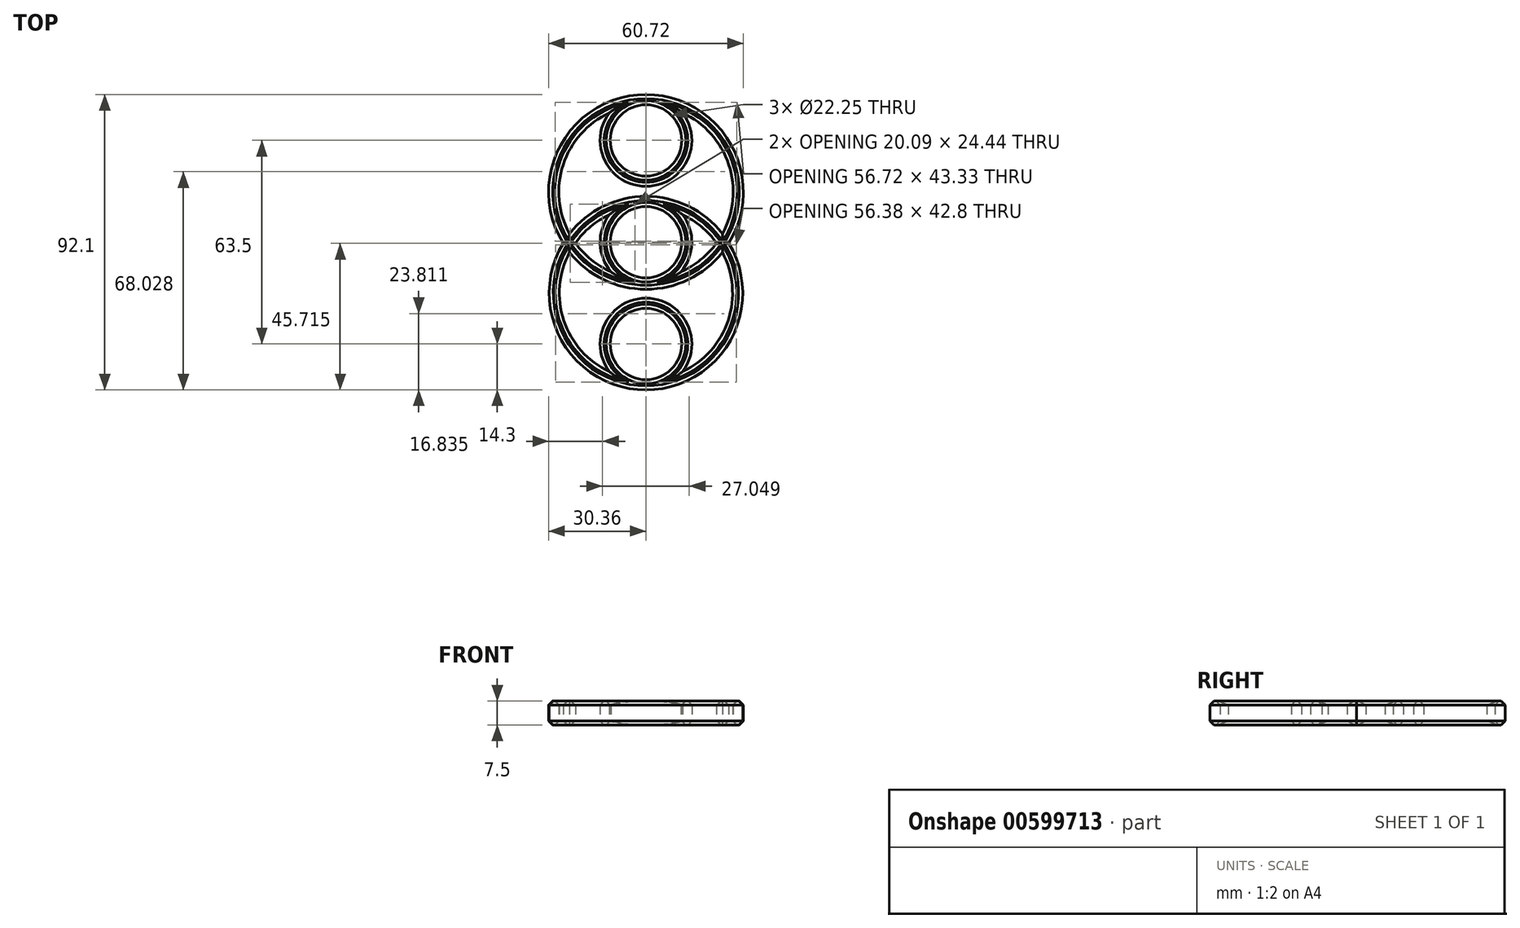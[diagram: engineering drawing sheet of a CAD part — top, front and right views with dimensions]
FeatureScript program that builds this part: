
annotation { "Feature Type Name" : "Feature", "Feature Type Description" : "" }
export const myFeature = defineFeature(function(context is Context, id is Id, definition is map)
    precondition{}
    {
        {
            var Q0;
            Q0=qCreatedBy(makeId("Top.planeOp"),FACE);
            var sketch = newSketch(context, id + "F0", { "sketchPlane" : qUnion([Q0])});
            skCircle(sketch, "E0", {"center": v(0, 0) * mm, "radius": 11.12 * mm});
            skCircle(sketch, "E1", {"center": v(0, 31.75) * mm, "radius": 11.12 * mm});
            skCircle(sketch, "E2", {"center": v(0, -31.75) * mm, "radius": 11.12 * mm});
            skCircle(sketch, "E3", {"center": v(0, 31.75) * mm, "radius": 14.3 * mm});
            skCircle(sketch, "E4", {"center": v(0, 0) * mm, "radius": 14.3 * mm});
            skCircle(sketch, "E5", {"center": v(0, -31.75) * mm, "radius": 14.3 * mm});
            skCircle(sketch, "E6", {"center": v(0, 15.69) * mm, "radius": 30.36 * mm});
            skCircle(sketch, "E7", {"center": v(0, 15.69) * mm, "radius": 27.19 * mm});
            skCircle(sketch, "E8", {"center": v(0, -15.88) * mm, "radius": 30.18 * mm});
            skCircle(sketch, "E9", {"center": v(0, -15.88) * mm, "radius": 27 * mm});
            skSolve(sketch);
        }
        {
            var Q0;
            Q0 = qSketchRegion(id + "F0", true);
            var Q1;
            {var subQ0=sQuery(id+"F0.wireOp",EDGE,"E1");Q1=makeQuery(id+"F0.imprint","IMPRINT",FACE,{"disambiguationData":[TD([[makeQuery(id+"F0.imprint","IMPRINT",EDGE,{"derivedFrom":subQ0}),-1.0]])]});}
            var Q2;
            {var subQ0=sQuery(id+"F0.wireOp",EDGE,"E8");var subQ1=sQuery(id+"F0.wireOp",EDGE,"E4");var subQ2=makeQuery(id+"F0.imprint","INTERSECT",VERTEX,{"derivedFrom":[subQ1,subQ0]});Q2=makeQuery(id+"F0.imprint","IMPRINT",FACE,{"disambiguationData":[TD([[makeQuery(id+"F0.imprint","IMPRINT",EDGE,{"disambiguationData":[TD([[subQ2,1.0]])],"derivedFrom":subQ1}),-1.0]])]});}
            var Q3;
            {var subQ0=sQuery(id+"F0.wireOp",EDGE,"E4");var subQ1=makeQuery(id+"F0.imprint","INTERSECT",VERTEX,{"derivedFrom":[subQ0,sQuery(id+"F0.wireOp",EDGE,"E8")]});Q3=makeQuery(id+"F0.imprint","IMPRINT",FACE,{"disambiguationData":[TD([[makeQuery(id+"F0.imprint","IMPRINT",EDGE,{"disambiguationData":[TD([[subQ1,1.0]])],"derivedFrom":subQ0}),1.0]])]});}
            var Q4;
            {var subQ0=sQuery(id+"F0.wireOp",EDGE,"E8");var subQ1=sQuery(id+"F0.wireOp",EDGE,"E4");var subQ2=makeQuery(id+"F0.imprint","INTERSECT",VERTEX,{"derivedFrom":[subQ1,subQ0]});Q4=makeQuery(id+"F0.imprint","IMPRINT",FACE,{"disambiguationData":[TD([[makeQuery(id+"F0.imprint","IMPRINT",EDGE,{"disambiguationData":[TD([[subQ2,-1.0]])],"derivedFrom":subQ1}),-1.0]])]});}
            var Q5;
            {var subQ0=sQuery(id+"F0.wireOp",EDGE,"E7");var subQ1=sQuery(id+"F0.wireOp",EDGE,"E0");var subQ2=makeQuery(id+"F0.imprint","INTERSECT",VERTEX,{"derivedFrom":[subQ1,subQ0]});Q5=makeQuery(id+"F0.imprint","IMPRINT",FACE,{"disambiguationData":[TD([[makeQuery(id+"F0.imprint","IMPRINT",EDGE,{"disambiguationData":[TD([[subQ2,1.0]])],"derivedFrom":subQ1}),-1.0]])]});}
            var Q6;
            {var subQ0=sQuery(id+"F0.wireOp",EDGE,"E7");var subQ1=sQuery(id+"F0.wireOp",EDGE,"E0");var subQ2=makeQuery(id+"F0.imprint","INTERSECT",VERTEX,{"derivedFrom":[subQ1,subQ0]});Q6=makeQuery(id+"F0.imprint","IMPRINT",FACE,{"disambiguationData":[TD([[makeQuery(id+"F0.imprint","IMPRINT",EDGE,{"disambiguationData":[TD([[subQ2,-1.0]])],"derivedFrom":subQ1}),-1.0]])]});}
            var Q7;
            {var subQ0=sQuery(id+"F0.wireOp",EDGE,"E7");var subQ1=sQuery(id+"F0.wireOp",EDGE,"E4");var subQ2=makeQuery(id+"F0.imprint","INTERSECT",VERTEX,{"disambiguationData":[OD(0.0)],"derivedFrom":[subQ1,subQ0]});Q7=makeQuery(id+"F0.imprint","IMPRINT",FACE,{"disambiguationData":[TD([[makeQuery(id+"F0.imprint","IMPRINT",EDGE,{"disambiguationData":[TD([[subQ2,-1.0]])],"derivedFrom":subQ1}),1.0]])]});}
            var Q8;
            {var subQ0=sQuery(id+"F0.wireOp",EDGE,"E7");var subQ1=sQuery(id+"F0.wireOp",EDGE,"E4");var subQ2=makeQuery(id+"F0.imprint","INTERSECT",VERTEX,{"disambiguationData":[OD(0.0)],"derivedFrom":[subQ1,subQ0]});Q8=makeQuery(id+"F0.imprint","IMPRINT",FACE,{"disambiguationData":[TD([[makeQuery(id+"F0.imprint","IMPRINT",EDGE,{"disambiguationData":[TD([[subQ2,-1.0]])],"derivedFrom":subQ1}),-1.0]])]});}
            var Q9;
            {var subQ0=sQuery(id+"F0.wireOp",EDGE,"E2");Q9=makeQuery(id+"F0.imprint","IMPRINT",FACE,{"disambiguationData":[TD([[makeQuery(id+"F0.imprint","IMPRINT",EDGE,{"derivedFrom":subQ0}),-1.0]])]});}
            extrude(context, id + "F1", {"entities" : qUnion([Q0, Q1, Q2, Q3, Q4, Q5, Q6, Q7, Q8, Q9]), "depth" : 7.5 * mm, "offsetDistance" : 25.4 * mm});
        }
        {
            var Q0;
            Q0=makeQuery(id+"F1.opExtrude","CAP_FACE",FACE,{"disambiguationData":[OSD([sQuery(id+"F0.wireOp",EDGE,"E0"),sQuery(id+"F0.wireOp",EDGE,"E1"),sQuery(id+"F0.wireOp",EDGE,"E2"),sQuery(id+"F0.wireOp",EDGE,"E3"),sQuery(id+"F0.wireOp",EDGE,"E4"),sQuery(id+"F0.wireOp",EDGE,"E5"),sQuery(id+"F0.wireOp",EDGE,"E6"),sQuery(id+"F0.wireOp",EDGE,"E7"),sQuery(id+"F0.wireOp",EDGE,"E8"),sQuery(id+"F0.wireOp",EDGE,"E9")])],"isStart":false});
            var Q1;
            Q1=makeQuery(id+"F1.opExtrude","CAP_FACE",FACE,{"disambiguationData":[OSD([sQuery(id+"F0.wireOp",EDGE,"E0"),sQuery(id+"F0.wireOp",EDGE,"E1"),sQuery(id+"F0.wireOp",EDGE,"E2"),sQuery(id+"F0.wireOp",EDGE,"E3"),sQuery(id+"F0.wireOp",EDGE,"E4"),sQuery(id+"F0.wireOp",EDGE,"E5"),sQuery(id+"F0.wireOp",EDGE,"E6"),sQuery(id+"F0.wireOp",EDGE,"E7"),sQuery(id+"F0.wireOp",EDGE,"E8"),sQuery(id+"F0.wireOp",EDGE,"E9")])],"isStart":true});
            chamfer(context, id + "F2", {"entities" : qUnion([Q0, Q1]), "width" : 1.27 * mm, "tangentPropagation" : true});
        }
    });
